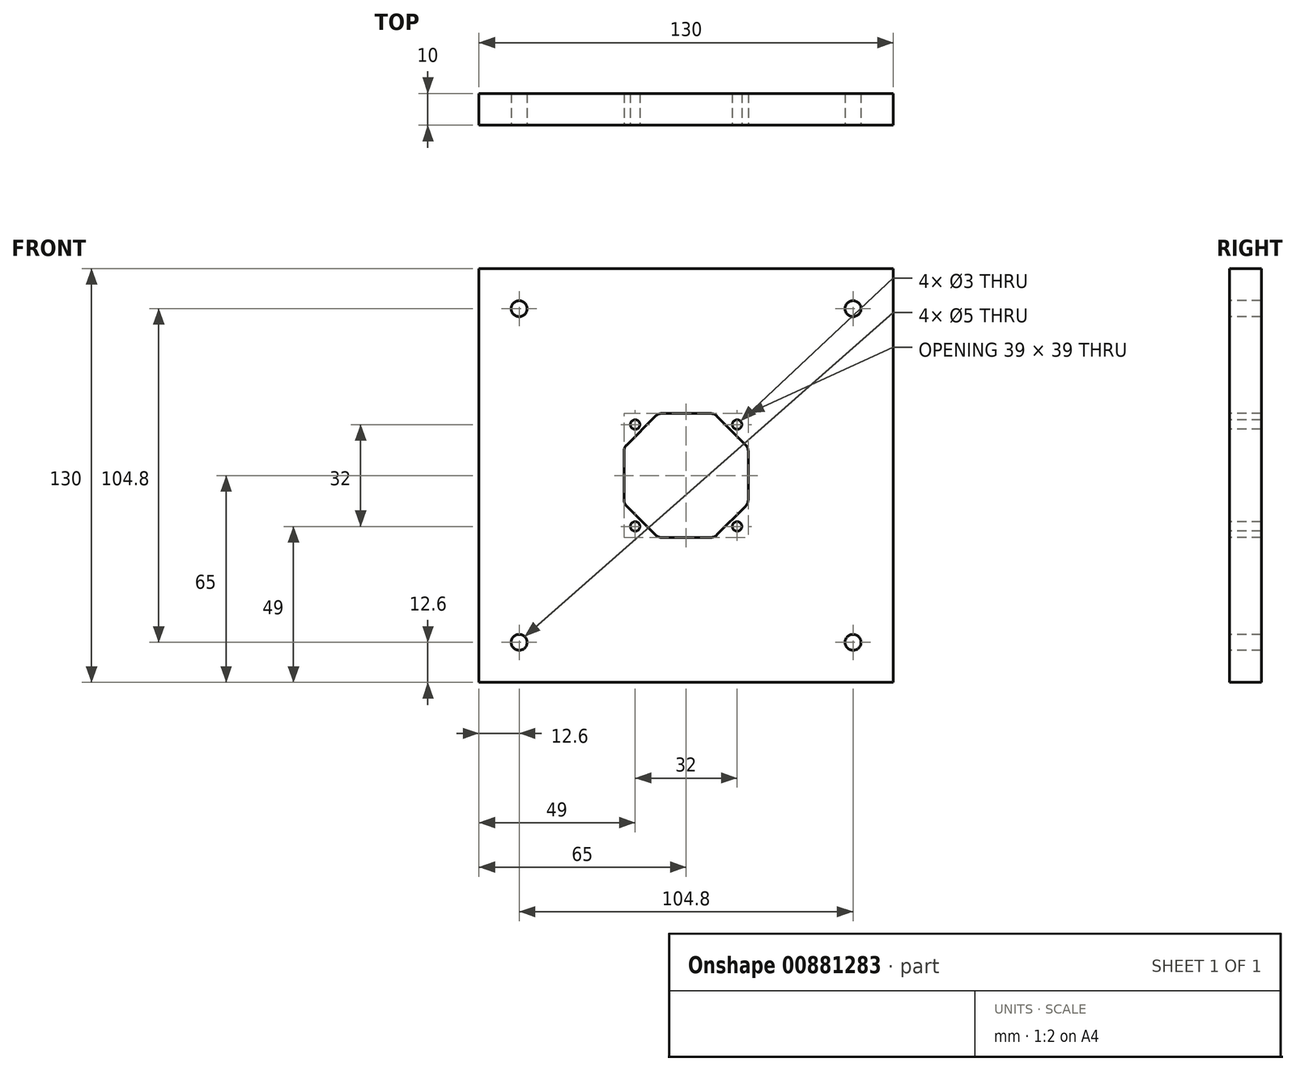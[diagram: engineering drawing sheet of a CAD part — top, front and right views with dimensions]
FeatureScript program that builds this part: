
annotation { "Feature Type Name" : "Feature", "Feature Type Description" : "" }
export const myFeature = defineFeature(function(context is Context, id is Id, definition is map)
    precondition{}
    {
        {
            var Q0;
            Q0=qCreatedBy(makeId("Front.planeOp"),FACE);
            var sketch = newSketch(context, id + "F0", { "sketchPlane" : qUnion([Q0])});
            skLineSegment(sketch, "E0", {"start": v(0, 131.99) * mm, "end": v(0, -133.67) * mm, "construction": true});
            skLineSegment(sketch, "E1", {"start": v(-164.48, 0) * mm, "end": v(165.6, 0) * mm, "construction": true});
            skLineSegment(sketch, "E2.bottom", {"start": v(-65, 65) * mm, "end": v(65, 65) * mm});
            skLineSegment(sketch, "E2.top", {"start": v(-65, -65) * mm, "end": v(65, -65) * mm});
            skLineSegment(sketch, "E2.left", {"start": v(-65, 65) * mm, "end": v(-65, -65) * mm});
            skLineSegment(sketch, "E2.right", {"start": v(65, 65) * mm, "end": v(65, -65) * mm});
            skSolve(sketch);
        }
        {
            var Q0;
            Q0 = qSketchRegion(id + "F0", true);
            extrude(context, id + "F1", {"entities" : qUnion([Q0]), "depth" : 10 * mm, "offsetDistance" : 25 * mm});
        }
        {
            var Q0;
            Q0=makeQuery(id+"F1.opExtrude","CAP_FACE",FACE,{"disambiguationData":[OSD([sQuery(id+"F0.wireOp",EDGE,"E2.bottom"),sQuery(id+"F0.wireOp",EDGE,"E2.top"),sQuery(id+"F0.wireOp",EDGE,"E2.left"),sQuery(id+"F0.wireOp",EDGE,"E2.right")])],"isStart":false});
            var sketch = newSketch(context, id + "F2", { "sketchPlane" : qUnion([Q0])});
            skLineSegment(sketch, "E3", {"start": v(0, 40.84) * mm, "end": v(0, -42.76) * mm, "construction": true});
            skLineSegment(sketch, "E4", {"start": v(-55.07, 0) * mm, "end": v(57.8, 0) * mm, "construction": true});
            skLineSegment(sketch, "E5", {"start": v(-8.8, 19.5) * mm, "end": v(8.8, 19.5) * mm});
            skLineSegment(sketch, "E6", {"start": v(-19.5, 8.77) * mm, "end": v(-19.5, -8.77) * mm});
            skLineSegment(sketch, "E7.MirrorCS", {"start": v(-8.8, -19.5) * mm, "end": v(8.8, -19.5) * mm});
            skLineSegment(sketch, "E8.MirrorCS", {"start": v(19.5, 8.77) * mm, "end": v(19.5, -8.77) * mm});
            skLineSegment(sketch, "E9", {"start": v(-8.8, 19.5) * mm, "end": v(-19.5, 8.77) * mm});
            skLineSegment(sketch, "E10", {"start": v(8.8, 19.5) * mm, "end": v(19.5, 8.77) * mm});
            skLineSegment(sketch, "E11", {"start": v(19.5, -8.77) * mm, "end": v(8.8, -19.5) * mm});
            skLineSegment(sketch, "E12", {"start": v(-19.5, -8.77) * mm, "end": v(-8.8, -19.5) * mm});
            skSolve(sketch);
        }
        {
            var Q0;
            Q0 = qSketchRegion(id + "F2", true);
            extrude(context, id + "F3", {"entities" : qUnion([Q0]), "operationType" : NewBodyOperationType.REMOVE, "endBound" : BoundingType.UP_TO_NEXT, "oppositeDirection" : true, "depth" : 25 * mm, "offsetDistance" : 25 * mm});
        }
        {
            var Q0;
            Q0=makeQuery(id+"F1.opExtrude","CAP_FACE",FACE,{"disambiguationData":[OSD([sQuery(id+"F0.wireOp",EDGE,"E2.bottom"),sQuery(id+"F0.wireOp",EDGE,"E2.top"),sQuery(id+"F0.wireOp",EDGE,"E2.left"),sQuery(id+"F0.wireOp",EDGE,"E2.right")])],"isStart":false});
            var sketch = newSketch(context, id + "F4", { "sketchPlane" : qUnion([Q0])});
            skLineSegment(sketch, "E13", {"start": v(0, 77.3) * mm, "end": v(0, -77.25) * mm, "construction": true});
            skLineSegment(sketch, "E14", {"start": v(-79.63, 0) * mm, "end": v(79.27, 0) * mm, "construction": true});
            skCircle(sketch, "E15", {"center": v(16, 16) * mm, "radius": 1.5 * mm});
            skCircle(sketch, "E16.MirrorC", {"center": v(16, -16) * mm, "radius": 1.5 * mm});
            skCircle(sketch, "E17.MirrorC", {"center": v(-16, 16) * mm, "radius": 1.5 * mm});
            skCircle(sketch, "E18.MirrorC", {"center": v(-16, -16) * mm, "radius": 1.5 * mm});
            skSolve(sketch);
        }
        {
            var Q0;
            Q0 = qSketchRegion(id + "F4", true);
            extrude(context, id + "F5", {"entities" : qUnion([Q0]), "operationType" : NewBodyOperationType.REMOVE, "endBound" : BoundingType.UP_TO_NEXT, "oppositeDirection" : true, "depth" : 25 * mm, "offsetDistance" : 25 * mm});
        }
        {
            var Q0;
            Q0=makeQuery(id+"F1.opExtrude","CAP_FACE",FACE,{"disambiguationData":[OSD([sQuery(id+"F0.wireOp",EDGE,"E2.bottom"),sQuery(id+"F0.wireOp",EDGE,"E2.top"),sQuery(id+"F0.wireOp",EDGE,"E2.left"),sQuery(id+"F0.wireOp",EDGE,"E2.right")])],"isStart":false});
            var sketch = newSketch(context, id + "F6", { "sketchPlane" : qUnion([Q0])});
            skLineSegment(sketch, "E19", {"start": v(0, 81.15) * mm, "end": v(0, -85.4) * mm, "construction": true});
            skPoint(sketch, "E19.endSnap0", {"position": v(0, -65) * mm});
            skLineSegment(sketch, "E20", {"start": v(-86.25, 0) * mm, "end": v(90.43, 0) * mm, "construction": true});
            skCircle(sketch, "E21", {"center": v(52.4, 52.4) * mm, "radius": 2.5 * mm});
            skCircle(sketch, "E22.MirrorC", {"center": v(52.4, -52.4) * mm, "radius": 2.5 * mm});
            skCircle(sketch, "E23.MirrorC", {"center": v(-52.4, 52.4) * mm, "radius": 2.5 * mm});
            skCircle(sketch, "E24.MirrorC", {"center": v(-52.4, -52.4) * mm, "radius": 2.5 * mm});
            skSolve(sketch);
        }
        {
            var Q0;
            Q0 = qSketchRegion(id + "F6", true);
            extrude(context, id + "F7", {"entities" : qUnion([Q0]), "operationType" : NewBodyOperationType.REMOVE, "endBound" : BoundingType.UP_TO_NEXT, "oppositeDirection" : true, "depth" : 25 * mm, "offsetDistance" : 25 * mm});
        }
        {
            var Q0;
            Q0=makeQuery(id+"F3.boolean.opBoolean","COPY",EDGE,{"derivedFrom":makeQuery(id+"F3.opExtrude","SWEPT_EDGE",EDGE,{"disambiguationData":[OSD([sQuery(id+"F2.wireOp",EDGE,"E6"),sQuery(id+"F2.wireOp",EDGE,"E9")])]})});
            var Q1;
            Q1=makeQuery(id+"F3.boolean.opBoolean","COPY",EDGE,{"derivedFrom":makeQuery(id+"F3.opExtrude","SWEPT_EDGE",EDGE,{"disambiguationData":[OSD([sQuery(id+"F2.wireOp",EDGE,"E5"),sQuery(id+"F2.wireOp",EDGE,"E9")])]})});
            var Q2;
            Q2=makeQuery(id+"F3.boolean.opBoolean","COPY",EDGE,{"derivedFrom":makeQuery(id+"F3.opExtrude","SWEPT_EDGE",EDGE,{"disambiguationData":[OSD([sQuery(id+"F2.wireOp",EDGE,"E6"),sQuery(id+"F2.wireOp",EDGE,"E12")])]})});
            var Q3;
            Q3=makeQuery(id+"F3.boolean.opBoolean","COPY",EDGE,{"derivedFrom":makeQuery(id+"F3.opExtrude","SWEPT_EDGE",EDGE,{"disambiguationData":[OSD([sQuery(id+"F2.wireOp",EDGE,"E7.MirrorCS"),sQuery(id+"F2.wireOp",EDGE,"E12")])]})});
            var Q4;
            Q4=makeQuery(id+"F3.boolean.opBoolean","COPY",EDGE,{"derivedFrom":makeQuery(id+"F3.opExtrude","SWEPT_EDGE",EDGE,{"disambiguationData":[OSD([sQuery(id+"F2.wireOp",EDGE,"E7.MirrorCS"),sQuery(id+"F2.wireOp",EDGE,"E11")])]})});
            var Q5;
            Q5=makeQuery(id+"F3.boolean.opBoolean","COPY",EDGE,{"derivedFrom":makeQuery(id+"F3.opExtrude","SWEPT_EDGE",EDGE,{"disambiguationData":[OSD([sQuery(id+"F2.wireOp",EDGE,"E8.MirrorCS"),sQuery(id+"F2.wireOp",EDGE,"E11")])]})});
            var Q6;
            Q6=makeQuery(id+"F3.boolean.opBoolean","COPY",EDGE,{"derivedFrom":makeQuery(id+"F3.opExtrude","SWEPT_EDGE",EDGE,{"disambiguationData":[OSD([sQuery(id+"F2.wireOp",EDGE,"E8.MirrorCS"),sQuery(id+"F2.wireOp",EDGE,"E10")])]})});
            var Q7;
            Q7=makeQuery(id+"F3.boolean.opBoolean","COPY",EDGE,{"derivedFrom":makeQuery(id+"F3.opExtrude","SWEPT_EDGE",EDGE,{"disambiguationData":[OSD([sQuery(id+"F2.wireOp",EDGE,"E5"),sQuery(id+"F2.wireOp",EDGE,"E10")])]})});
            fillet(context, id + "F8", {"entities" : qUnion([Q0, Q1, Q2, Q3, Q4, Q5, Q6, Q7]), "radius" : 3 * mm, "tangentPropagation" : true, "allowEdgeOverflow" : false});
        }
    });
